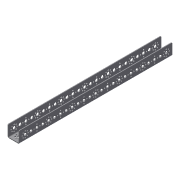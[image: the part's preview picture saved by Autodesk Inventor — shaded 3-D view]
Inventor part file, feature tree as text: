
AUTODESK INVENTOR PART (.ipt)
format: ipt  version: 2013 (Build 170138000, 138)  size: 556,544 bytes
history: native  units: in
note: dims shown in document units (in); Inventor stores cm internally (conversion verified against a paired STEP export)
features: hole x28, other x5, sketch x3
ambient origin geometry x8: Origin, YZ Plane, XZ Plane, XY Plane, X Axis, Y Axis, Z Axis, Center Point
bodies: Solid1 (feature_tree)
feature tree (36):
  other  "Tetrix Channel 416mm.ipt"
  other  "Blocks"
  hole  "Hole Pattern 4"  [1 undecoded]
  hole  "Hole Pattern 8"  [1 undecoded]
  other  "416 mm hole pattern"
  other  "Solid1::Tetrix Channel 416mm.ipt"
  other  "TaggingFeature1"
  sketch  "Sketch1"  dims[d0=0.3937in]
  sketch  "Sketch2"  dims[d1=16.378in d3=0.6299in d4=0.1457in d6=0.6299in d8=0.6299in d9=0.6299in d10=0.315in d13=0.1457in d14=0.315in d15=3.1496in d20=0.6299in d21=0.6299in d22=0.6299in d23=0.6299in d25=0.6299in d26=0.6299in d27=0.0787in d28=0.0787in d29=0.0394in d30=0.1575in d31=0.0787in d32=1.2598in d33=90.0deg d34=0.0787in d35=0.315in d36=0.0787in d37=0.0787in d38=0.6299in d39=0.6299in d40=0.6299in d41=0.6299in d42=0.6299in d43=0.6299in d45=0.6299in d47=0.0in d48=0.0787in d17=360.0deg]
  sketch  "Sketch3"
  hole  "Hole Pattern 4:1"  [1 undecoded]
  hole  "Hole Pattern 8:1"  [1 undecoded]
  hole  "Hole Pattern 8:2"  [1 undecoded]
  hole  "Hole Pattern 4:2"  [1 undecoded]
  hole  "Hole Pattern 8:3"  [1 undecoded]
  hole  "Hole Pattern 4:3"  [1 undecoded]
  hole  "Hole Pattern 8:4"  [1 undecoded]
  hole  "Hole Pattern 4:4"  [1 undecoded]
  hole  "Hole Pattern 8:5"  [1 undecoded]
  hole  "Hole Pattern 8:6"  [1 undecoded]
  hole  "Hole Pattern 4:5"  [1 undecoded]
  hole  "Hole Pattern 8:7"  [1 undecoded]
  hole  "Hole Pattern 4:6"  [1 undecoded]
  hole  "Hole Pattern 4:1_1"  [1 undecoded]
  hole  "Hole Pattern 8:1_1"  [1 undecoded]
  hole  "Hole Pattern 8:2_1"  [1 undecoded]
  hole  "Hole Pattern 4:2_1"  [1 undecoded]
  hole  "Hole Pattern 8:3_1"  [1 undecoded]
  hole  "Hole Pattern 4:3_1"  [1 undecoded]
  hole  "Hole Pattern 8:4_1"  [1 undecoded]
  hole  "Hole Pattern 4:4_1"  [1 undecoded]
  hole  "Hole Pattern 8:5_1"  [1 undecoded]
  hole  "Hole Pattern 8:6_1"  [1 undecoded]
  hole  "Hole Pattern 4:5_1"  [1 undecoded]
  hole  "Hole Pattern 8:7_1"  [1 undecoded]
  hole  "Hole Pattern 4:6_1"  [1 undecoded]
note: 28 required parameter values undecoded (feature->parameter linkage not recoverable at this tier; creation-order binding heuristic only, values carry confidence <= 0.55)
